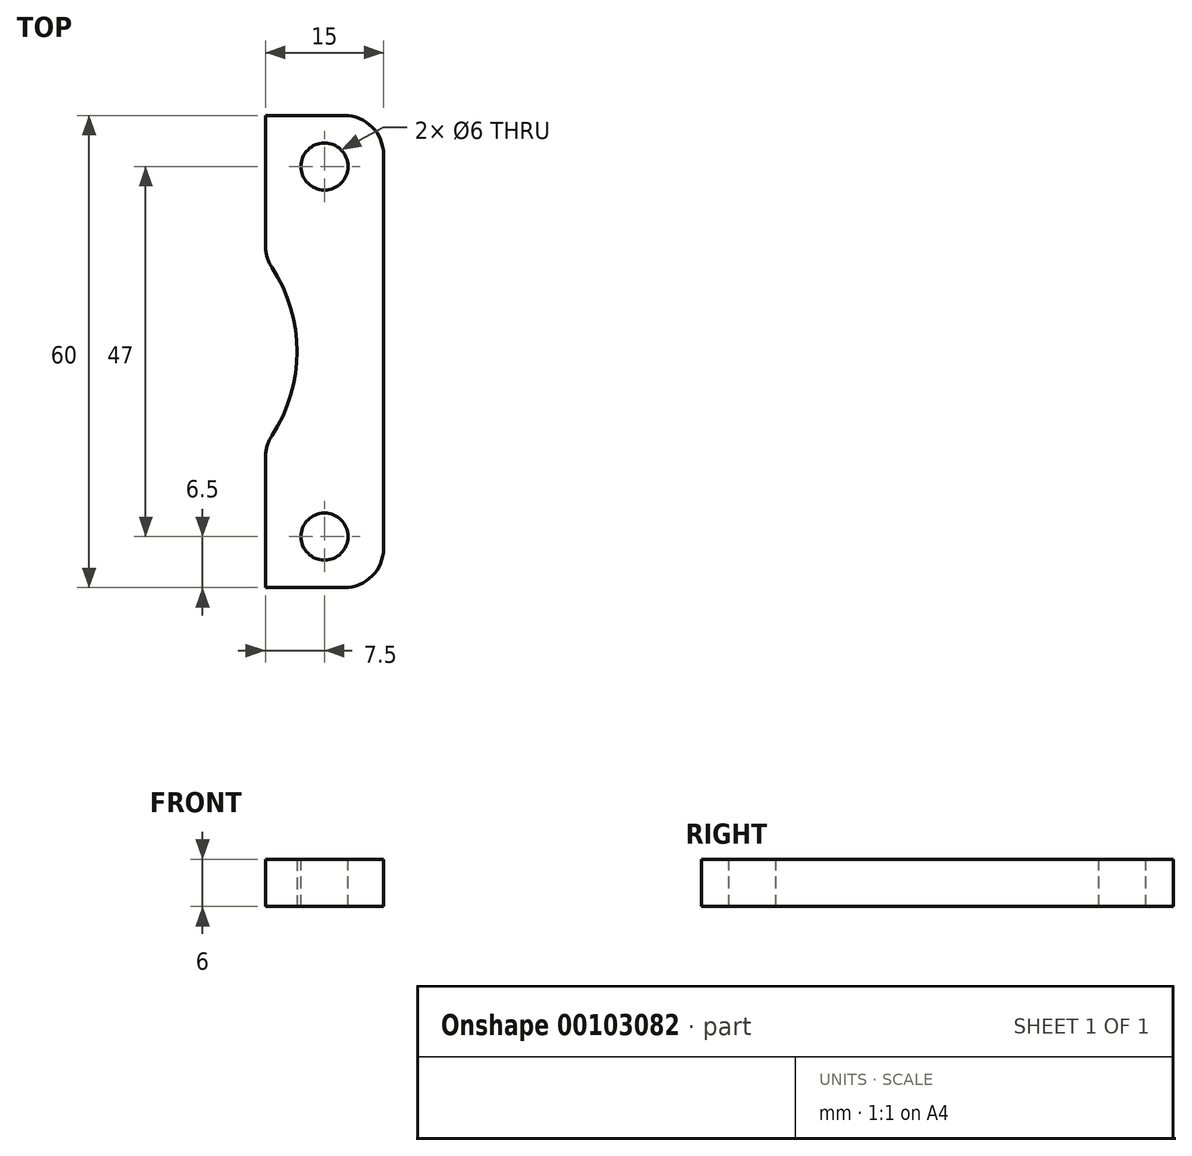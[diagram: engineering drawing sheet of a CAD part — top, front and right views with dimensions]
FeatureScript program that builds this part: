
annotation { "Feature Type Name" : "Feature", "Feature Type Description" : "" }
export const myFeature = defineFeature(function(context is Context, id is Id, definition is map)
    precondition{}
    {
        {
            var Q0;
            Q0=qCreatedBy(makeId("Top.planeOp"),FACE);
            var sketch = newSketch(context, id + "F0", { "sketchPlane" : qUnion([Q0])});
            skLineSegment(sketch, "E0.bottom", {"start": v(7.5, 30) * mm, "end": v(-7.5, 30) * mm});
            skLineSegment(sketch, "E0.top", {"start": v(7.5, -30) * mm, "end": v(-7.5, -30) * mm});
            skLineSegment(sketch, "E0.left", {"start": v(7.5, 30) * mm, "end": v(7.5, -30) * mm});
            skLineSegment(sketch, "E0.right", {"start": v(-7.5, 30) * mm, "end": v(-7.5, 11.83) * mm});
            skPoint(sketch, "E0.middle", {"position": v(0, 0) * mm});
            skArc(sketch, "E1", {"start": v(-7.5, -11.83) * mm, "mid": v(-3.5, 0) * mm, "end": v(-7.5, 11.83) * mm});
            skLineSegment(sketch, "E2.trimOffspring", {"start": v(-7.5, -11.83) * mm, "end": v(-7.5, -30) * mm});
            skSolve(sketch);
        }
        {
            var Q0;
            Q0=makeQuery(id+"F0.imprint","IMPRINT",FACE,{"disambiguationData":[TD([[makeQuery(id+"F0.imprint","IMPRINT",EDGE,{"derivedFrom":sQuery(id+"F0.wireOp",EDGE,"E0.bottom")}),1.0]])]});
            extrude(context, id + "F1", {"entities" : qUnion([Q0]), "depth" : 6 * mm});
        }
        {
            var Q0;
            Q0=makeQuery(id+"F1.opExtrude","CAP_FACE",FACE,{"disambiguationData":[OSD([sQuery(id+"F0.wireOp",EDGE,"E0.bottom"),sQuery(id+"F0.wireOp",EDGE,"E0.top"),sQuery(id+"F0.wireOp",EDGE,"E0.left"),sQuery(id+"F0.wireOp",EDGE,"E0.right"),sQuery(id+"F0.wireOp",EDGE,"E1"),sQuery(id+"F0.wireOp",EDGE,"E2.trimOffspring")])],"isStart":false});
            var sketch = newSketch(context, id + "F2", { "sketchPlane" : qUnion([Q0])});
            skPoint(sketch, "E3", {"position": v(0, 23.5) * mm});
            skPoint(sketch, "E4", {"position": v(0, -23.5) * mm});
            skSolve(sketch);
        }
        {
            var Q0;
            Q0=sQuery(id+"F2.wireOp",VERTEX,"E3");
            var Q1;
            Q1=sQuery(id+"F2.wireOp",VERTEX,"E4");
            var Q2;
            Q2=makeQuery(id+"F1.opExtrude","SWEPT_BODY",BODY,{"disambiguationData":[OSD([sQuery(id+"F0.wireOp",EDGE,"E0.bottom"),sQuery(id+"F0.wireOp",EDGE,"E0.top"),sQuery(id+"F0.wireOp",EDGE,"E0.left"),sQuery(id+"F0.wireOp",EDGE,"E0.right"),sQuery(id+"F0.wireOp",EDGE,"E1"),sQuery(id+"F0.wireOp",EDGE,"E2.trimOffspring")])]});
            hole(context, id + "F3", {"style" : HoleStyle.SIMPLE, "endStyle" : HoleEndStyle.THROUGH, "holeDiameter" : 6 * mm, "locations" : qUnion([Q0, Q1]), "scope" : qUnion([Q2]), "isTappedThrough" : true});
        }
        {
            var Q0;
            Q0=makeQuery(id+"F1.opExtrude","SWEPT_EDGE",EDGE,{"disambiguationData":[OSD([sQuery(id+"F0.wireOp",EDGE,"E0.bottom"),sQuery(id+"F0.wireOp",EDGE,"E0.left")])]});
            var Q1;
            Q1=makeQuery(id+"F1.opExtrude","SWEPT_EDGE",EDGE,{"disambiguationData":[OSD([sQuery(id+"F0.wireOp",EDGE,"E0.top"),sQuery(id+"F0.wireOp",EDGE,"E0.left")])]});
            var Q2;
            Q2=makeQuery(id+"F1.opExtrude","SWEPT_EDGE",EDGE,{"disambiguationData":[OSD([sQuery(id+"F0.wireOp",EDGE,"E1"),sQuery(id+"F0.wireOp",EDGE,"E2.trimOffspring")])]});
            var Q3;
            Q3=makeQuery(id+"F1.opExtrude","SWEPT_EDGE",EDGE,{"disambiguationData":[OSD([sQuery(id+"F0.wireOp",EDGE,"E0.right"),sQuery(id+"F0.wireOp",EDGE,"E1")])]});
            fillet(context, id + "F4", {"entities" : qUnion([Q0, Q1, Q2, Q3]), "radius" : 5 * mm, "tangentPropagation" : true, "allowEdgeOverflow" : false});
        }
    });
